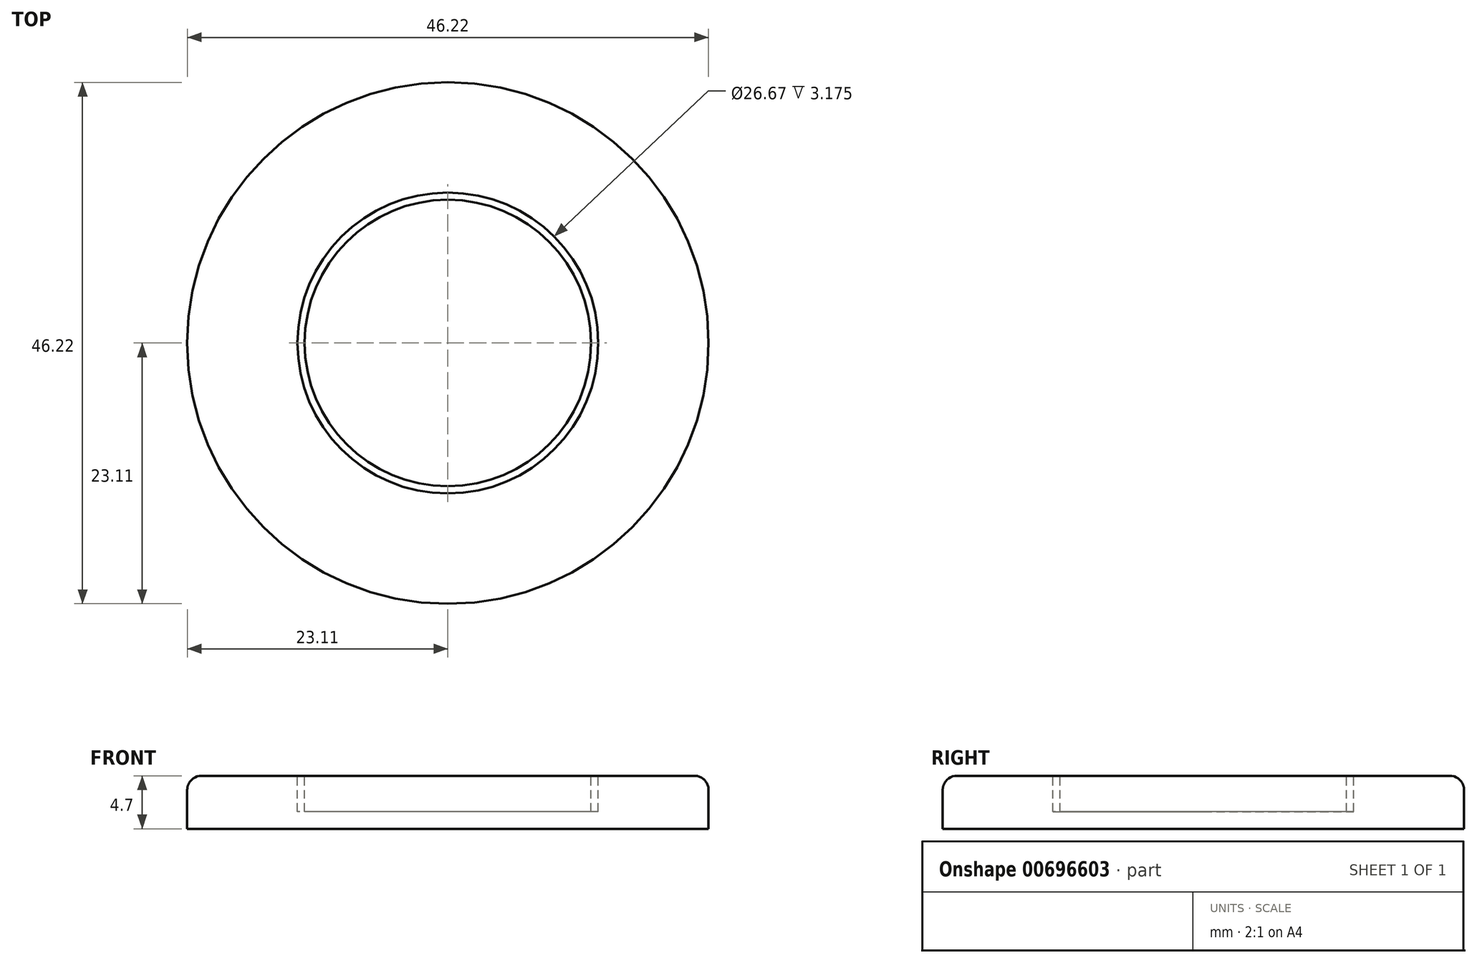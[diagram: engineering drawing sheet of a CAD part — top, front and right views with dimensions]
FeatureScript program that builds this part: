
annotation { "Feature Type Name" : "Feature", "Feature Type Description" : "" }
export const myFeature = defineFeature(function(context is Context, id is Id, definition is map)
    precondition{}
    {
        {
            var Q0;
            Q0=qCreatedBy(makeId("Top.planeOp"),FACE);
            var sketch = newSketch(context, id + "F0", { "sketchPlane" : qUnion([Q0])});
            skCircle(sketch, "E0", {"center": v(0, 0) * mm, "radius": 23.11 * mm});
            skSolve(sketch);
        }
        {
            var Q0;
            Q0=qSketchRegion(id+"F0",true);
            extrude(context, id + "F1", {"entities" : qUnion([Q0]), "oppositeDirection" : true, "depth" : 4.7 * mm, "offsetDistance" : 25.4 * mm});
        }
        {
            var Q0;
            Q0=makeQuery(id+"F1.opExtrude","CAP_EDGE",EDGE,{"disambiguationData":[OSD([sQuery(id+"F0.wireOp",EDGE,"E0")])],"isStart":true});
            fillet(context, id + "F2", {"entities" : qUnion([Q0]), "radius" : 1.27 * mm, "tangentPropagation" : true, "allowEdgeOverflow" : false});
        }
        {
            var Q0;
            Q0=makeQuery(id+"F1.opExtrude","CAP_FACE",FACE,{"disambiguationData":[OSD([sQuery(id+"F0.wireOp",EDGE,"E0")])],"isStart":true});
            var sketch = newSketch(context, id + "F3", { "sketchPlane" : qUnion([Q0])});
            skCircle(sketch, "E1", {"center": v(0, 0) * mm, "radius": 13.34 * mm});
            skCircle(sketch, "E2", {"center": v(0, 0) * mm, "radius": 12.7 * mm});
            skSolve(sketch);
        }
        {
            var Q0;
            Q0=qSketchRegion(id+"F3",true);
            extrude(context, id + "F4", {"entities" : qUnion([Q0]), "operationType" : NewBodyOperationType.REMOVE, "oppositeDirection" : true, "depth" : 3.17 * mm, "offsetDistance" : 25.4 * mm});
        }
    });
